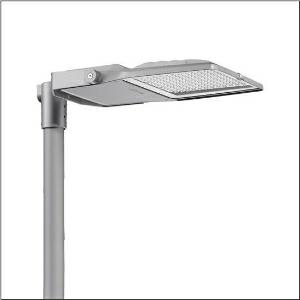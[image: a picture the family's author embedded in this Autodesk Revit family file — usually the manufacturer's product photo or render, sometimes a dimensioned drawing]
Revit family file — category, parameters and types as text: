
# Revit family: floodlight_fl_21_iq_midi___pl61_5xa7781e2c3a_352e
name_source: partatom
category: Lighting Fixtures
units: mm (PartAtom-declared; Revit-internal decimal feet)

## family parameters
Cut with Voids When Loaded = No
Host = Face
Light Source = No
Part Type = Normal
Room Calculation Point = No
Round Connector Dimension = Use Diameter
Shared = No

## types (1)
- --- (1 x LED, 26360 lm, 208.1 W, 3000K)
    Apparent Load = 208 VA
    CIE Flux Codes = 33 65 98 100 100
    Color Rendering = 70
    Color Temperature = 3000K
    Default Elevation = 1800 mm
    Description = Floodlight FL 21 iQ midi, floodlight, primary light control with lens, of PMMA, primary optical cover: protective disc, of toughened safety glass, transparent, light distribution: PL61, light emission: direct distribution, installation type: surface-mounted, LED, High Power LED, rated luminous flux: 26.360lm, luminous efficacy: 127lm/W, light colour: 730, colour temperature: 3000K, control gear: iQ Comfort/DALI, control: optimised constant luminous flux control (CLO 2.0), Desk-Remote (wireless, voltage-free reading and setting of iQ features in the workshop via application-optimized NFC function/RFID function), Light-Fading, Smart-Wire, Night-Set, Lumen-Switch, Temp-Guard, Auto-Match, with terminal, 6-pole, mains connection: 220..240V, AC, 50/60Hz, start of lifetime: 208W, end of service life: 227W, reduction: 90W, luminaire housing, of diecast aluminium, powder-coated, Siteco® metallic grey (DB 702S), corrosivity category C5 mid according to DIN EN ISO 12944, suitable for swimming pools, chlorine-resistant, sealing non-destructively replaceable, please order mast flange separately, mast bracket, of steel, galvanised, powder-coated, Siteco® metallic grey (DB 702S), protection rating (complete): IP66, insulation class (complete): insulation class II (safety insulation), certification: CE, ENEC, VDE, protection symbol: D, impact resistance: IK08, permissible operating ambient temperature: -40..+40°C, permissible operating ambient temperature for outdoor applications: -40..+50°C, standard: DIN EN 12944, LABS conformity tested according to VDMA 24364:2018-05, packaging unit: 1 piece

Light Distribution: PL61
    Height = 76 mm
    Lamp = 1 x LED
    Lamp Light Flux = 26360 lm
    Lamp Power = 208.1 W
    Lamp count = 1
    Length = 657 mm
    Luminous efficacy = 127 lm/W
    Manufacturer = Siteco
    ModVariant = No
    Model = 5XA7781E2C3A
    Number of Poles = 1
    OnlyDefault = Yes
    Power Factor = 1
    Product Name = Floodlight FL 21 iQ midi | PL61
    Product group = floodlight | pylon annexe
    ProductGroupID = 6200
    Protection Class = Protection class II
    Protection Degree = IP 66
    RLX_Detail_Level = 1
    RLX_Emergency_Light_Flux = 0 lm
    RLX_Emergency_Type = 0
    RLX_Emergency_Type_DB = No
    RlxData = <blob elided: 153729 chars, md5=1504a464>
    Socket = socket
    Standby Power = 0 W
    System Light Flux = 26360 lm
    System Power = 208 W
    Type Comments = factory setting: luminous flux: 100 % | dim-lin: 254 | 710 mA
    Type Image = l_1007123.jpg
    URL = http://relux.com
    VarID = @adj_108938
    Voltage = 0 V
    Weight = 0.00 kg
    Width = 442 mm

## geometry (parser evidence)
native form markers: Blend x4, Sweep x13
no freeform markers — native parametric forms only
